# Revit family: QF_ELECTROLUXPROFESSIONAL_1LSNTL_WN6-11_E
name_source: partatom
category: Attrezzature speciali
units: mm (PartAtom-declared; Revit-internal decimal feet)

## family parameters
Basato su piano di lavoro = No
Condiviso = No
Punto di calcolo locali = No
Quota connettore circolare = Usa diametro
Sempre verticale = Sì
Taglio con vuoti quando caricato = No
Tipo di parte = Normale

## types (29) — shared parameters
Depth = 697 mm  [stored 2.28675 ft]
Depth Actual = 700 mm  [stored 2.29659 ft]
Height = 1218.8 mm  [stored 3.99869 ft]
Height Actual = 1220 mm  [stored 4.00262 ft]
Latent Heat Output = 0.0
Length Actual = 720 mm  [stored 2.3622 ft]
Modello = WN6-11
Produttore = Electrolux Professional
Sensible Heat Output = 0.0
URL = www.electroluxprofessional.com
Weight = 152
Width = 720 mm  [stored 2.3622 ft]
zero-valued in all types: Gas KW, Prospetto di default, Steam Pounds per Hour

## per-type parameters (varying)
| type | Cycle | Descrizione | Item Number | Phase | Volts | Watts |
| 9867730182 | 50 Hz | WASHER WN6-11 11KG EL 10KW 380-415/50/3N COMPASS PRO 6G01 ML 2xWATER POWDER+5xLIQ. VALV.OPEN SST/SILVER 2.I/O DISCON. ST | 1LA24H | 3 | 415 V | 10400 W |
| 9867730029 | 50 Hz | WASHER WN6-11 11KG NO HEAT 200/50/60/3 COMPASS PRO 6L41 JP,EN 2xWATER 5xLIQ. VALV.OPEN SILVER CM. JPY+KRW 2.I/O DISCON. | 1L822X | 3 | 200 V | 800 W |
| 9867730152 | 60 Hz | WASHER WN6-11 11KG EL 10KW 440/60/3 COMPASS PRO 6G01 ML 2xWATER POWDER VALV.OPEN SILVER TRAFO DISCON. STOP | 1L0GJ9 | 3 | 440 V | 10500 W |
| 9867730157 | 50 Hz | WASHER WN6-11 11KG EL 7,5KW 220-240/50/1N COMPASS PRO 6G07 ML 2xWATER POWDER+5xLIQ. VALV.OPEN SST/SILVER 2.I/O DISCON. S | 1LA22D | 1 | 240 V | 7900 W |
| 9867730240 | 60 Hz | WASHER WN6-11 11KG EL 10KW 440/60/3 COMPASS PRO 6G07 ML 2xWATER POWDER PUMP SST/SILVER TRAFO DISCON. STOP | 1L0H7E | 3 | 440 V | 10500 W |
| 9867730107 | 50 Hz | WASHER WN6-11 11KG EL 10KW 380-415/220-240/50/3N/1 COMPASS PRO 6G01 ML 2xWATER POWDER+5xLIQ. VALV.OPEN SILVER 2.I/O DISC | 1L0GBJ | 3 | 415 V | 10400 W |
| 9867730056 | 50 Hz | WASHER WN6-11 11KG EL 10KW 380-415/50/3N COMPASS PRO 6G01 ML 2xWATER POWDER VALV.OPEN SILVER DISCON. STOP | 1L0G8M | 3 | 415 V | 8800 W |
| 9867730174 | 50 Hz | WASHER WN6-11 11KG EL 10KW 220-240/50/3 COMPASS PRO 6G01 ML 2xWATER POWDER+5xLIQ. VALV.OPEN SILVER 2.I/O DISCON. STOP | 1L0GTG | 3 | 240 V | 10400 W |
| 9867730075 | 50 Hz | WASHER WN6-11 11KG NO HEAT 220-240/50/1N COMPASS PRO 6L01 ML 2xWATER POWDER+5xLIQ. VALV.OPEN SILVER EXT.PM. 2.I/O DISCON | 1L823S | 1 | 240 V | 800 W |
| 9867730206 | 60 Hz | WASHER WN6-11 11KG EL 10KW 220-240/60/1 COMPASS PRO 6G07 SE 2xWATER POWDER+5xLIQ. PUMP SST/SILVER 2.I/O DISCON. STOP | 1LSPNH | 1 | 240 V | 10400 W |
| 9867730090 | 60 Hz | WASHER WN6-11 11KG EL 10KW 440/60/3 COMPASS PRO 6G01 ML 2xWATER POWDER VALV.OPEN SST/SILVER TRAFO DISCON. STOP | 1L8240 | 3 | 440 V | 10500 W |
| 9867730189 | 60 Hz | WASHER WN6-11 11KG EL 7,5KW 220-240/60/3 COMPASS PRO 6G07 ML 2xWATER POWDER+5xLIQ. VALV.OPEN SST/SILVER 2.I/O DISCON. ST | 1L0GWP | 3 | 240 V | 7900 W |
| 9867730179 | 60 Hz | WASHER WN6-11 11KG EL 10KW 440/60/3 COMPASS PRO 6G01 ML 2xWATER POWDER+5xLIQ. VALV.OPEN SST/SILVER 2.I/O TRAFO DISCON. S | 1L0GUR | 3 | 440 V | 10500 W |
| 9867730169 | 60 Hz | WASHER WN6-11 11KG NO HEAT 220-240/60/3 COMPASS PRO 6L01 ML 2xWATER POWDER VALV.OPEN SILVER DISCON. | 1L0GPY | 3 | 220 V | 800 W |
| 9867730030 | 50 Hz | WASHER WN6-11 11KG NO HEAT 200/50/60/3 COMPASS PRO 6G41 JP,EN 2xWATER POWDER+5xLIQ. VALV.OPEN SILVER SL.DRUM 2.I/O DISCO | 1L822Y | 3 | 200 V | 800 W |
| 9867730126 | 50 Hz | WASHER WN6-11 11KG EL 10KW 380-415/50/3N COMPASS PRO 6H01 ML 2xWATER POWDER+5xLIQ. VALV.OPEN SST/SILVER 2.I/O DISCON. ST | 1LSP9K | 3 | 415 V | 10400 W |
| 9867730264 | 50 Hz | WASHER WN6-11 11KG EL 10KW 220-240/50/3 COMPASS PRO 6G07 ML 2xWATER POWDER+5xLIQ. VALV.OPEN SST/SILVER 2.I/O DISCON. STO | 1LT6CC | 3 | 240 V | 8900 W |
| 9867730217 | 50 Hz | WASHER WN6-11 11KG EL 7,5KW 380-415/50/3 COMPASS PRO 6G07 ML 2xWATER POWDER+5xLIQ. VALV.OPEN SILVER 2.I/O TRAFO DISCON. | 1LA25P | 3 | 415 V | 7900 W |
| 9867730032 | 50 Hz | WASHER WN6-11 11KG EL 10KW 380-415/50/3 COMPASS PRO 6G01 ML 2xWATER POWDER VALV.OPEN SST/SILVER TRAFO DISCON. STOP | 1L822Z | 3 | 415 V | 8800 W |
| 9867730110 | 50 Hz | WASHER WN6-11 11KG NO HEAT 220-240/50/1N COMPASS PRO 6G01 ML 2xWATER POWDER+5xLIQ. VALV.OPEN SILVER 2.I/O DISCON. STOP | 1L0GC8 | 1 | 240 V | 800 W |
| 9867730091 | 60 Hz | WASHER WN6-11 11KG EL 10KW 440/60/3 COMPASS PRO 6G07 ML 2xWATER POWDER+5xLIQ. VALV.OPEN SILVER 2.I/O QC TRAFO DISCON. ST | 1LSP3M | 3 | 440 V | 10500 W |
| 9867730155 | 60 Hz | WASHER WN6-11 11KG EL 7,5KW 220-240/60/1N COMPASS PRO 6G07 ML 2xWATER POWDER+5xLIQ. VALV.OPEN SST/SILVER 2.I/O DISCON. S | 1L0GKH | 1 | 240 V | 10400 W |
| 9867730252 | 60 Hz | WASHER WN6-11 11KG NO HEAT 220/60/3 COMPASS PRO 6G01 CH-EN 2xWATER POWDER VALV.OPEN SILVER DISCON. STOP | 1L82CV | 3 | 220 V | 800 W |
| 9867730061 | 50 Hz | WASHER WN6-11 11KG EL 10KW 380-415/50/3N COMPASS PRO 6A01 ML 2xWATER POWDER VALV.OPEN SILVER DISCON. | 1LSP5C | 3 | 415 V | 10400 W |
| 9867730108 | 50 Hz | WASHER WN6-11 11KG EL 10KW 380-415/50/3N COMPASS PRO 6G01 ML 2xWATER POWDER+5xLIQ. VALV.OPEN SILVER 2.I/O DISCON. STOP | 1L0GBK | 3 | 415 V | 10400 W |
| 9867730202 | 60 Hz | WASHER WN6-11 11KG EL 10KW 480/60/3 COMPASS PRO 6G07 ML 2xWATER POWDER+5xLIQ. VALV.OPEN SILVER 2.I/O TRAFO DISCON. STOP | 1L828L | 3 | 480 V | 10500 W |
| 9867730031 | 50 Hz | WASHER WN6-11 11KG EL 7KW 200/50/60/3 COMPASS PRO 6G41 JP,EN 2xWATER POWDER+5xLIQ. VALV.OPEN SST/SILVER SL.DRUM 2.I/O DI | 1LSP3H | 3 | 200 V | 7400 W |
| 9867730232 | 50 Hz | WASHER WN6-11 11KG NO HEAT 200/50/60/3 COMPASS PRO 6L41 JP,EN 2xWATER 5xLIQ. VALV.OPEN SILVER SL.DRUM 2.I/O DISCON. | 1LT5ZN | 3 | 200 V | 800 W |
| 9867730245 | 60 Hz | WASHER WN6-11 11KG EL 9KW 115/60/3 COMPASS PRO 6G07 ML 2xWATER POWDER+5xLIQ. VALV.OPEN SILVER 2.I/O TRAFO DISCON. STOP | 1L0HC7 | 3 | 115 V | 9700 W |

note: [stored X ft] marks values corroborated as IEEE doubles in the binary element streams (Revit-internal decimal feet)

## geometry (parser evidence)
native form markers: Sweep x4
no freeform markers — native parametric forms only
